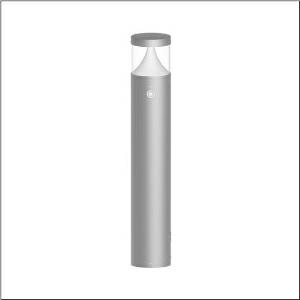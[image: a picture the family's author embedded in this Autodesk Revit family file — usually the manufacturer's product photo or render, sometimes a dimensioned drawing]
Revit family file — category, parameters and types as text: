
# Revit family: cl_31_poller_90_sensor_5cl444803
name_source: partatom
category: Lighting Fixtures
units: mm (PartAtom-declared; Revit-internal decimal feet)

## family parameters
Cut with Voids When Loaded = No
Host = Face
Light Source = No
Part Type = Normal
Room Calculation Point = No
Round Connector Dimension = Use Diameter
Shared = No

## types (1)
- --- (1 x LED, 1500 lm, 14 W, 3000K)
    Apparent Load = 14 VA
    CIE Flux Codes = 19 66 88 92 100
    Color Rendering = 80
    Color Temperature = 3000K
    Default Elevation = 1800 mm
    Description = CL 31 Bollard 90 Sensor, bollard luminaire, primary light control with lens, of PC, primary optical cover: cover panel, of PC, transparent, secondary light control with reflector, of PC, primary light characteristic: asymmetric, LED, rated luminous flux: 1.500lm, luminous efficacy: 107lm/W, light colour: 830, colour temperature: 3000K, control gear: DALI, with terminal, 5-pole, max. 2.5mm², mains connection: 220..240V, AC, 50/60Hz, rated input power: 14W, luminaire housing, of aluminium, powder-coated, SITECO metallic grey, diameter: 170mm, height: 900mm, PIR sensor, protection rating (complete): IP65, insulation class (complete): insulation class I (protective earthing), certification: CE, ENEC, impact resistance: IK08, permissible operating ambient temperature for outdoor applications: -20..+50°C, packaging unit: 1 piece
    Height = 200 mm  [stored 0.656168 ft]
    Lamp = 1 x LED
    Lamp Light Flux = 1500 lm
    Lamp Power = 14 W
    Lamp count = 1
    Length = 170 mm  [stored 0.557743 ft]
    Luminous efficacy = 107 lm/W
    Manufacturer = Siteco
    ModVariant = No
    Model = 5CL444803
    Mounting Place = Floor
    Mounting Type = Freestanding
    Number of Poles = 1
    OnlyDefault = Yes
    Power Factor = 1
    Product Name = CL 31 Poller 90 Sensor
    Product group = bollard luminaire
    ProductGroupID = 1304
    Protection Class = Protection class I
    Protection Degree = IP 65
    RLX_Detail_Level = 1
    RLX_Emergency_Light_Flux = 0 lm
    RLX_Emergency_Type = 0
    RLX_Emergency_Type_DB = No
    RlxData = <blob elided: 66045 chars, md5=72c97950>
    Socket = socket
    Standby Power = 0 W
    System Light Flux = 1500 lm
    System Power = 14 W
    Type Comments = factory setting: luminous flux: 100 % | dim-lin: 254 | 350 mA
    Type Image = l_1006897.jpg
    URL = http://relux.com
    VarID = @adj_192591
    Voltage = 0 V
    Weight = 0.00 kg
    Width = 0 mm  [stored 0 ft]

note: [stored X ft] marks values corroborated as IEEE doubles in the binary element streams (Revit-internal decimal feet)

## geometry (parser evidence)
native form markers: Blend x4, Sweep x9
no freeform markers — native parametric forms only
